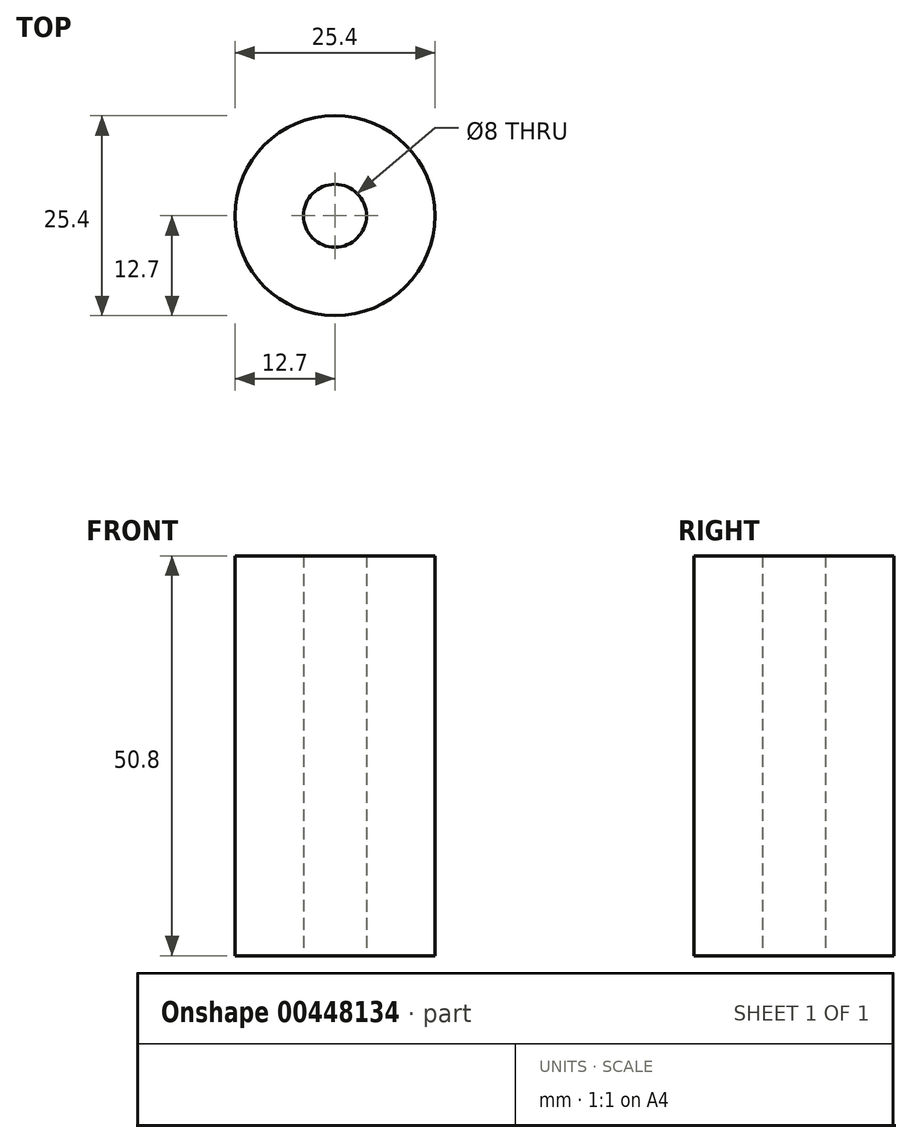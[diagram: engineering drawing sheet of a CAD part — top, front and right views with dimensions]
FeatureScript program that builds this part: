
annotation { "Feature Type Name" : "Feature", "Feature Type Description" : "" }
export const myFeature = defineFeature(function(context is Context, id is Id, definition is map)
    precondition{}
    {
        {
            var Q0;
            Q0=qCreatedBy(makeId("Top.planeOp"),FACE);
            var sketch = newSketch(context, id + "F0", { "sketchPlane" : qUnion([Q0])});
            skCircle(sketch, "E0", {"center": v(0, 0) * mm, "radius": 12.7 * mm});
            skSolve(sketch);
        }
        {
            var Q0;
            Q0=makeQuery(id+"F0.imprint","IMPRINT",FACE,{"disambiguationData":[TD([[makeQuery(id+"F0.imprint","IMPRINT",EDGE,{"derivedFrom":sQuery(id+"F0.wireOp",EDGE,"E0")}),1.0]])]});
            var sketch = newSketch(context, id + "F1", { "sketchPlane" : qUnion([Q0])});
            skCircle(sketch, "E1", {"center": v(0, 0) * mm, "radius": 4 * mm});
            skSolve(sketch);
        }
        {
            var Q0;
            Q0=makeQuery(id+"F0.imprint","IMPRINT",FACE,{"disambiguationData":[TD([[makeQuery(id+"F0.imprint","IMPRINT",EDGE,{"derivedFrom":sQuery(id+"F0.wireOp",EDGE,"E0")}),1.0]])]});
            extrude(context, id + "F2", {"entities" : qUnion([Q0]), "depth" : 50.8 * mm});
        }
        {
            var Q0;
            Q0 = qSketchRegion(id + "F1", true);
            extrude(context, id + "F3", {"entities" : qUnion([Q0]), "operationType" : NewBodyOperationType.REMOVE, "endBound" : BoundingType.THROUGH_ALL, "depth" : 50.8 * mm});
        }
    });
